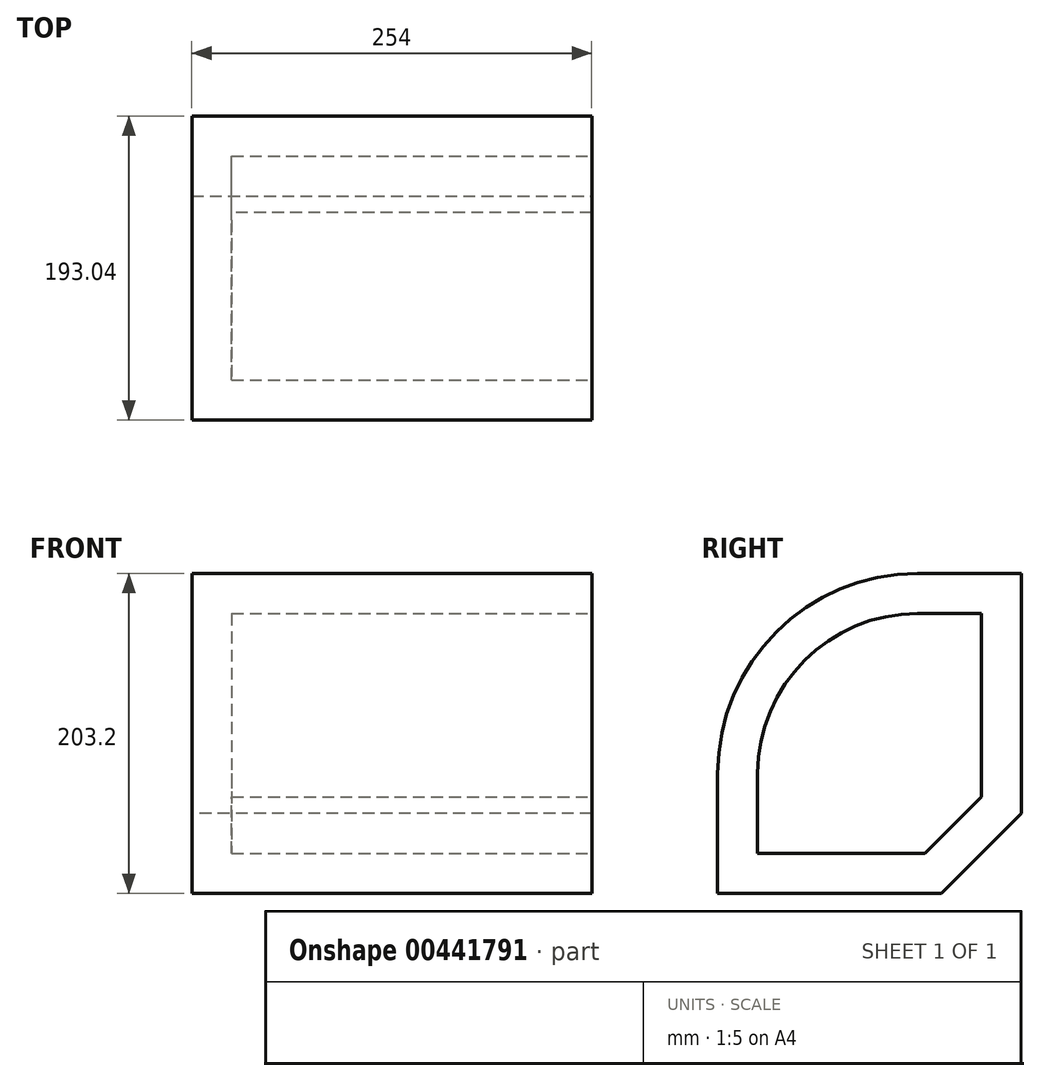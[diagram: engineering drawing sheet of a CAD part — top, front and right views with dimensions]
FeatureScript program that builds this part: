
annotation { "Feature Type Name" : "Feature", "Feature Type Description" : "" }
export const myFeature = defineFeature(function(context is Context, id is Id, definition is map)
    precondition{}
    {
        {
            var Q0;
            Q0=qCreatedBy(makeId("Front.planeOp"),FACE);
            var sketch = newSketch(context, id + "F0", { "sketchPlane" : qUnion([Q0])});
            skLineSegment(sketch, "E0.bottom", {"start": v(-123.53, 129.66) * mm, "end": v(130.47, 129.66) * mm});
            skLineSegment(sketch, "E0.top", {"start": v(-123.53, -73.54) * mm, "end": v(130.47, -73.54) * mm});
            skLineSegment(sketch, "E0.left", {"start": v(-123.53, 129.66) * mm, "end": v(-123.53, -73.54) * mm});
            skLineSegment(sketch, "E0.right", {"start": v(130.47, 129.66) * mm, "end": v(130.47, -73.54) * mm});
            skSolve(sketch);
        }
        {
            var Q0;
            Q0 = qSketchRegion(id + "F0", true);
            extrude(context, id + "F1", {"entities" : qUnion([Q0]), "depth" : 193.04 * mm});
        }
        {
            var Q0;
            Q0=makeQuery(id+"F1.opExtrude","CAP_EDGE",EDGE,{"disambiguationData":[OSD([sQuery(id+"F0.wireOp",EDGE,"E0.bottom")])],"isStart":false});
            fillet(context, id + "F2", {"entities" : qUnion([Q0]), "radius" : 127 * mm, "tangentPropagation" : true, "allowEdgeOverflow" : false});
        }
        {
            var Q0;
            Q0=makeQuery(id+"F1.opExtrude","CAP_EDGE",EDGE,{"disambiguationData":[OSD([sQuery(id+"F0.wireOp",EDGE,"E0.top")])],"isStart":true});
            chamfer(context, id + "F3", {"entities" : qUnion([Q0]), "width" : 50.8 * mm, "tangentPropagation" : true});
        }
        {
            var Q0;
            Q0=makeQuery(id+"F1.opExtrude","SWEPT_FACE",FACE,{"disambiguationData":[OSD([sQuery(id+"F0.wireOp",EDGE,"E0.right")])]});
            shell(context, id + "F4", {"entities" : qUnion([Q0]), "thickness" : 25.4 * mm});
        }
    });
